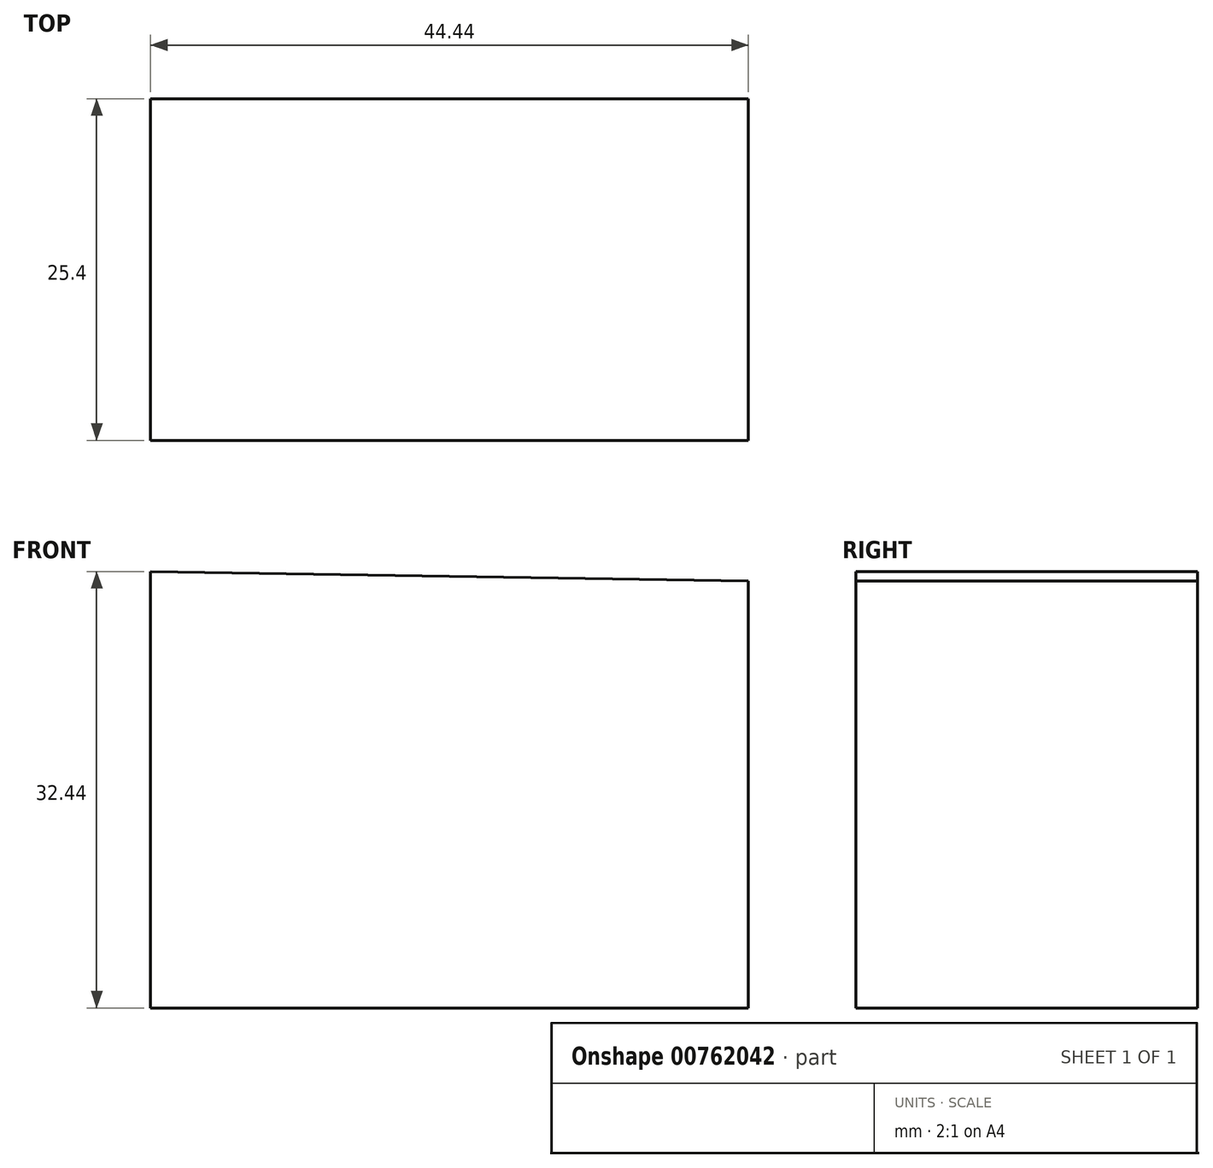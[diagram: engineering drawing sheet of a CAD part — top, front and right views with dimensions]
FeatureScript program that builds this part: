
annotation { "Feature Type Name" : "Feature", "Feature Type Description" : "" }
export const myFeature = defineFeature(function(context is Context, id is Id, definition is map)
    precondition{}
    {
        {
            var Q0;
            Q0=qCreatedBy(makeId("Front.planeOp"),FACE);
            var sketch = newSketch(context, id + "F0", { "sketchPlane" : qUnion([Q0])});
            skLineSegment(sketch, "E0", {"start": v(0, 32.44) * mm, "end": v(0, 0) * mm});
            skLineSegment(sketch, "E1", {"start": v(0, 0) * mm, "end": v(44.44, 0) * mm});
            skLineSegment(sketch, "E2", {"start": v(44.44, 0) * mm, "end": v(44.44, 31.75) * mm});
            skLineSegment(sketch, "E3", {"start": v(44.44, 31.75) * mm, "end": v(0, 32.44) * mm});
            skSolve(sketch);
        }
        {
            var Q0;
            Q0 = qSketchRegion(id + "F0", true);
            extrude(context, id + "F1", {"entities" : qUnion([Q0]), "depth" : 25.4 * mm, "offsetDistance" : 25.4 * mm});
        }
    });
